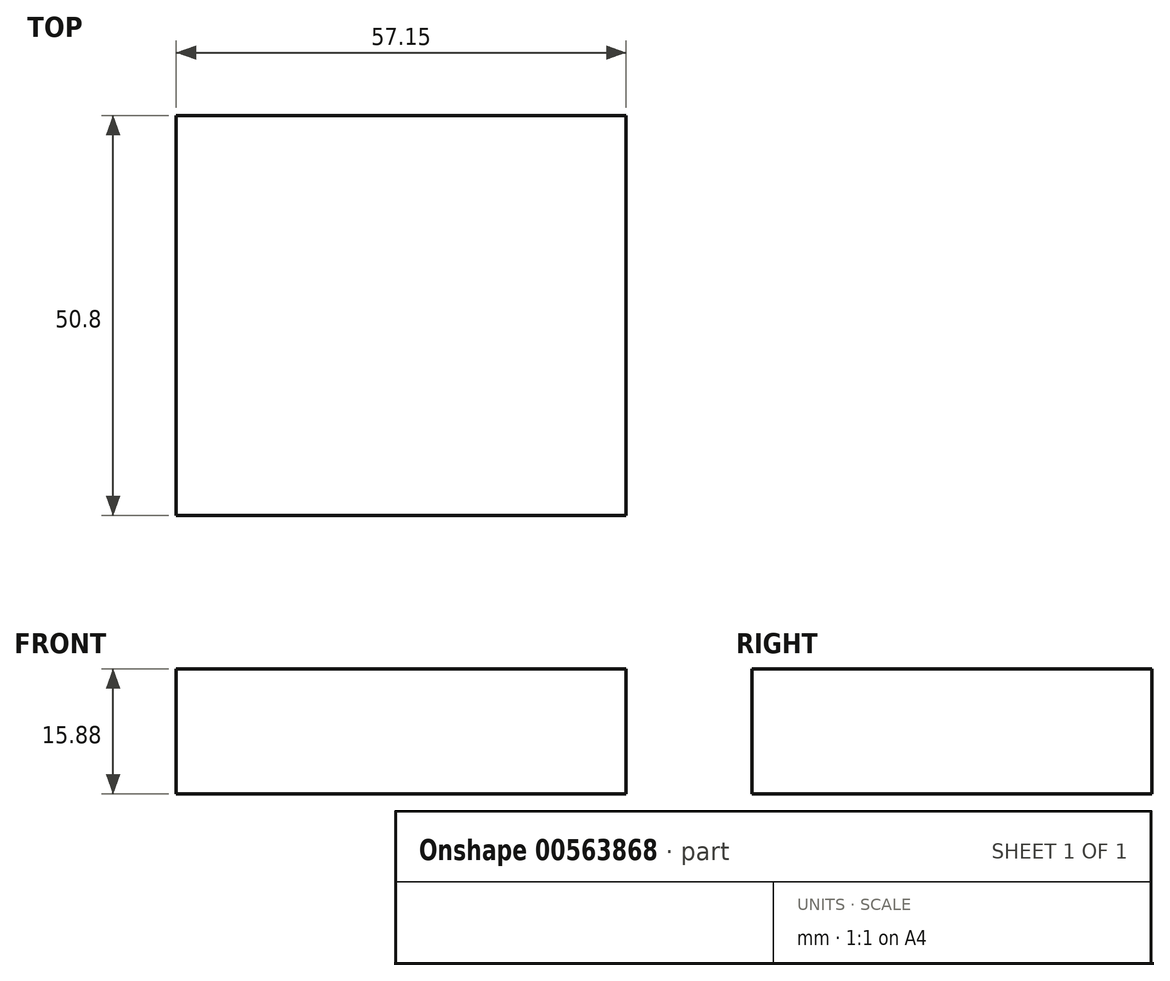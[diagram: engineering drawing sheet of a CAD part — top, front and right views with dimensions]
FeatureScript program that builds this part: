
annotation { "Feature Type Name" : "Feature", "Feature Type Description" : "" }
export const myFeature = defineFeature(function(context is Context, id is Id, definition is map)
    precondition{}
    {
        {
            var Q0;
            Q0=qCreatedBy(makeId("Top.planeOp"),FACE);
            var sketch = newSketch(context, id + "F0", { "sketchPlane" : qUnion([Q0])});
            skLineSegment(sketch, "E0.bottom", {"start": v(0, 0) * mm, "end": v(57.15, 0) * mm});
            skLineSegment(sketch, "E0.top", {"start": v(0, 50.8) * mm, "end": v(57.15, 50.8) * mm});
            skLineSegment(sketch, "E0.left", {"start": v(0, 0) * mm, "end": v(0, 50.8) * mm});
            skLineSegment(sketch, "E0.right", {"start": v(57.15, 0) * mm, "end": v(57.15, 50.8) * mm});
            skSolve(sketch);
        }
        {
            var Q0;
            Q0=makeQuery(id+"F0.imprint","IMPRINT",FACE,{"disambiguationData":[TD([[makeQuery(id+"F0.imprint","IMPRINT",EDGE,{"derivedFrom":sQuery(id+"F0.wireOp",EDGE,"E0.bottom")}),1.0]])]});
            extrude(context, id + "F1", {"entities" : qUnion([Q0]), "depth" : 15.88 * mm, "offsetDistance" : 25.4 * mm});
        }
    });
